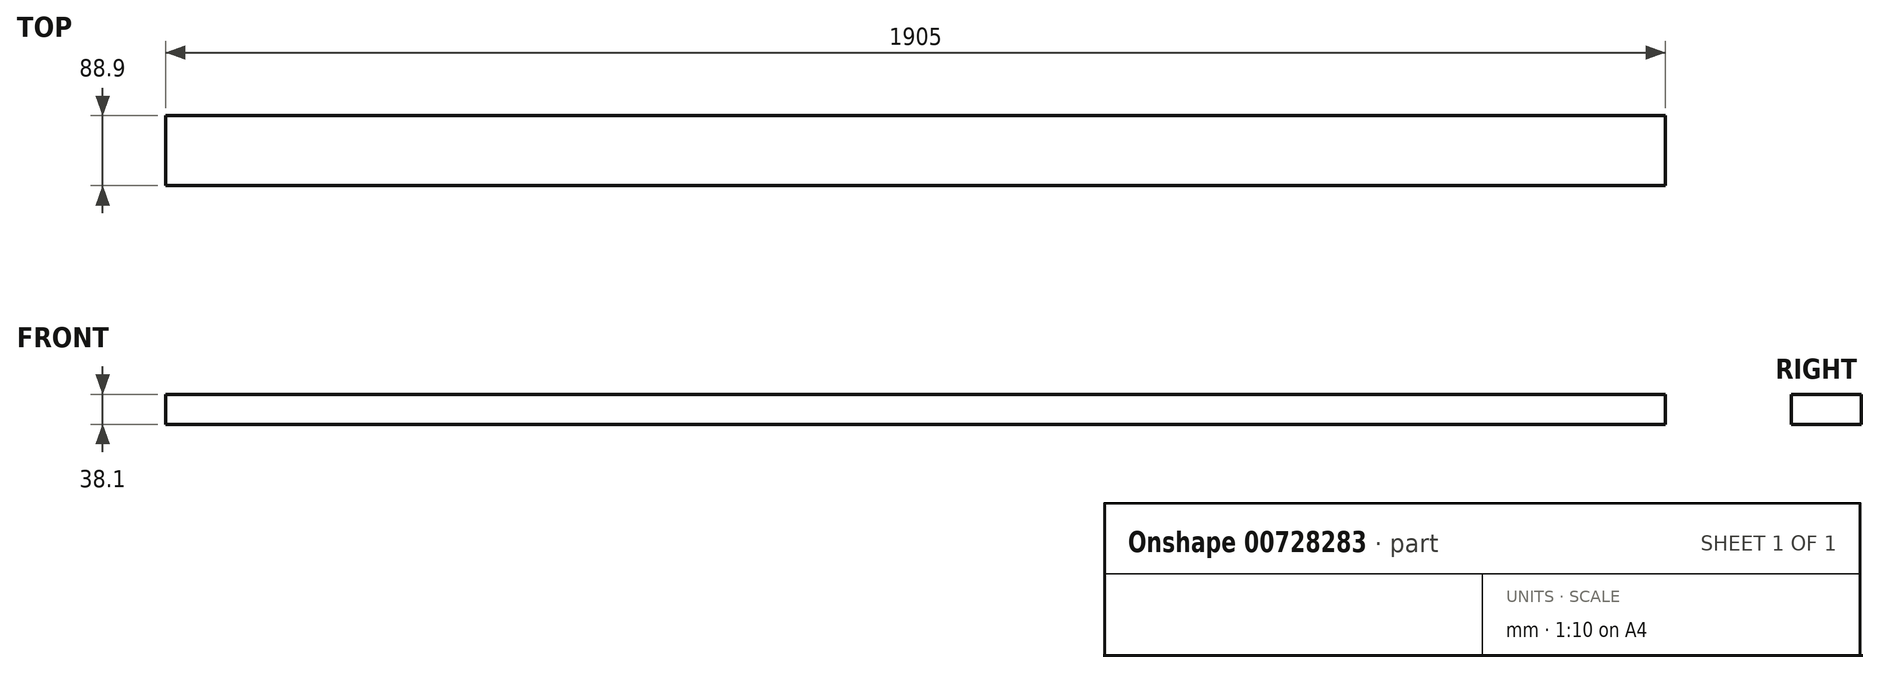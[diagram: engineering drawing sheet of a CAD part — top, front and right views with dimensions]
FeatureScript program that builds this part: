
annotation { "Feature Type Name" : "Feature", "Feature Type Description" : "" }
export const myFeature = defineFeature(function(context is Context, id is Id, definition is map)
    precondition{}
    {
        {
            var Q0;
            Q0=qCreatedBy(makeId("Front.planeOp"),FACE);
            var sketch = newSketch(context, id + "F0", { "sketchPlane" : qUnion([Q0])});
            skLineSegment(sketch, "E0.bottom", {"start": v(-952.5, -19.05) * mm, "end": v(952.5, -19.05) * mm});
            skLineSegment(sketch, "E0.top", {"start": v(-952.5, 19.05) * mm, "end": v(952.5, 19.05) * mm});
            skLineSegment(sketch, "E0.left", {"start": v(-952.5, -19.05) * mm, "end": v(-952.5, 19.05) * mm});
            skLineSegment(sketch, "E0.right", {"start": v(952.5, -19.05) * mm, "end": v(952.5, 19.05) * mm});
            skPoint(sketch, "E0.middle", {"position": v(0, 0) * mm});
            skSolve(sketch);
        }
        {
            var Q0;
            Q0=qSketchRegion(id+"F0",true);
            extrude(context, id + "F1", {"entities" : qUnion([Q0]), "depth" : 88.9 * mm, "offsetDistance" : 25.4 * mm});
        }
    });
